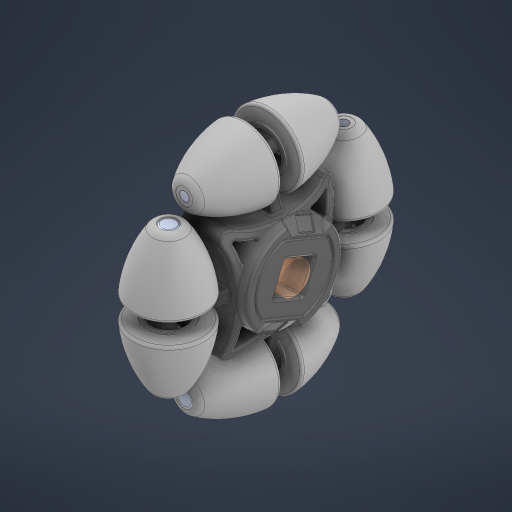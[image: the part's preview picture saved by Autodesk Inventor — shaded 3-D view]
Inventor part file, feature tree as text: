
AUTODESK INVENTOR PART (.ipt)
format: ipt  version: 2024.2 (Build 282272000, 272)  size: 4,720,128 bytes
history: native  units: in
note: dims shown in document units (in); Inventor stores cm internally (conversion verified against a paired STEP export)
features: other x16, sketch x1, extrude x1
ambient origin geometry x8: Origin, YZ Plane, XZ Plane, XY Plane, X Axis, Y Axis, Z Axis, Center Point
bodies: Solid1 (feature_tree), Solid2 (feature_tree), Solid3 (feature_tree), Solid4 (feature_tree), Solid5 (feature_tree), Solid6 (feature_tree), Solid7 (feature_tree), Solid8 (feature_tree), Solid9 (feature_tree), Solid10 (feature_tree), Solid11 (feature_tree), Solid12 (feature_tree), Solid13 (feature_tree), Solid14 (feature_tree), Solid15 (feature_tree)
feature tree (18):
  sketch  "Sketch1"  dims[d0=0.25in d1=0.3937in d2=0.0in]
  other  "Srf1"
  other  "276-9044-001-1-solid1"
  other  "276-9041-010-1-solid1"
  other  "276-9041-010-2-solid1"
  other  "Boss-Extrude1"
  parser-record x1  (decoder bookkeeping rows leaked as tree rows — omitted from the tree; the rows remain in map.json)
  other  "NONE:1"
  other  "CirPattern1[1]"
  other  "CirPattern1[2]"
  other  "CirPattern1[3]"
  other  "NONE:2"
  other  "NONE:3"
  other  "NONE:4"
  other  "NONE:5"
  other  "NONE:6"
  other  "NONE:7"
  extrude  "ExtrusionSrf1"  Depth=0.3937in TaperAngle=0.0deg
